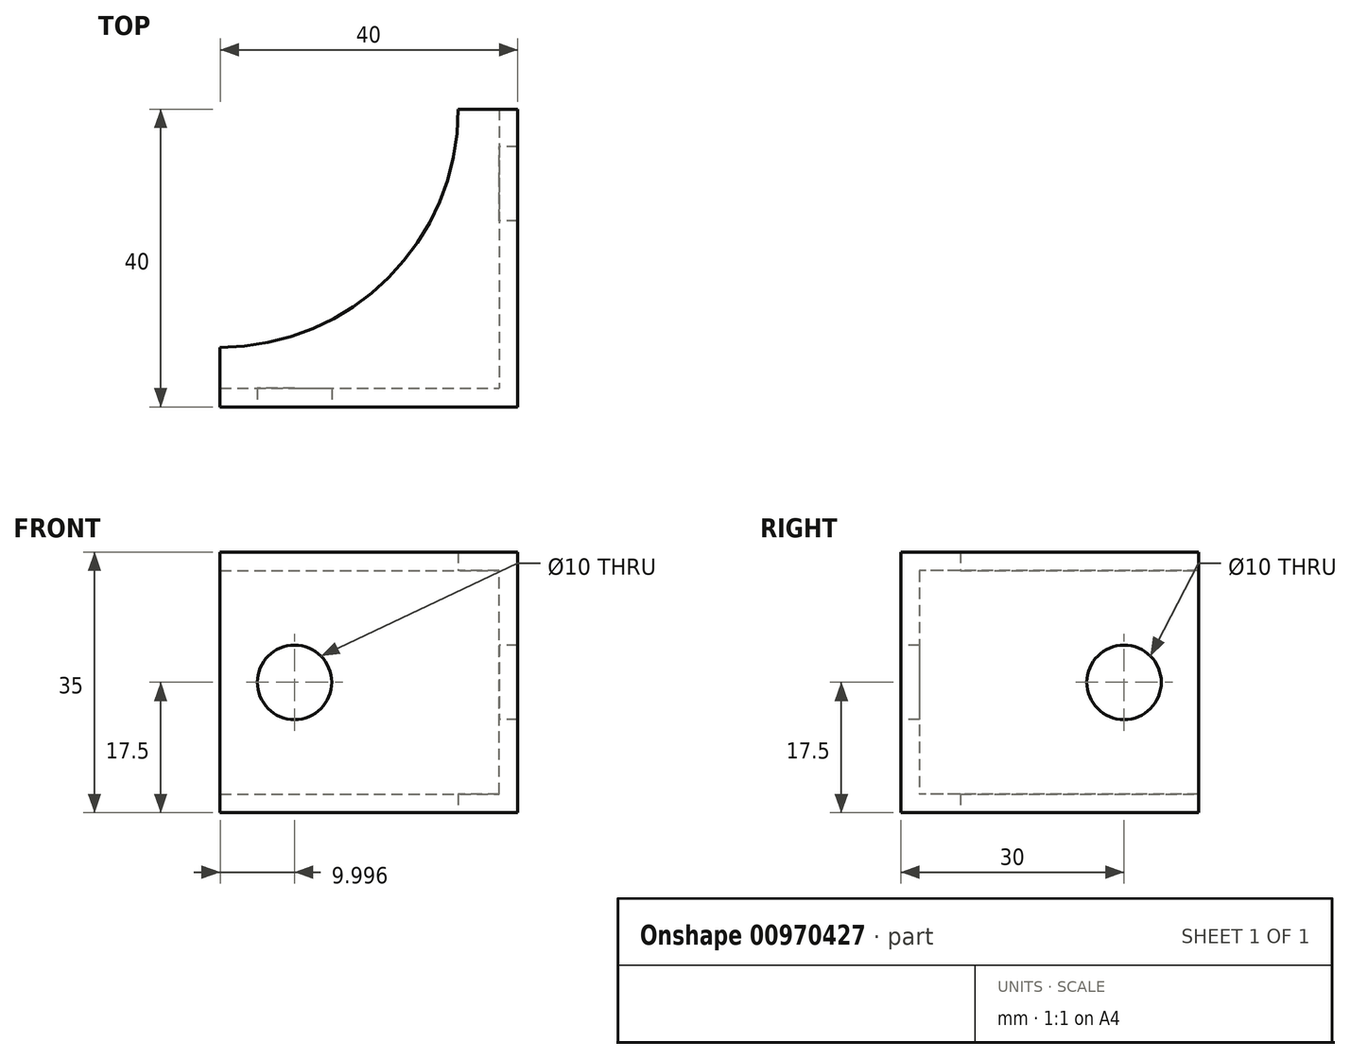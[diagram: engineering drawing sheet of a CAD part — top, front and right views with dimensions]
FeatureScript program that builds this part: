
annotation { "Feature Type Name" : "Feature", "Feature Type Description" : "" }
export const myFeature = defineFeature(function(context is Context, id is Id, definition is map)
    precondition{}
    {
        {
            var Q0;
            Q0=qCreatedBy(makeId("Top.planeOp"),FACE);
            var sketch = newSketch(context, id + "F0", { "sketchPlane" : qUnion([Q0])});
            skLineSegment(sketch, "E0.bottom", {"start": v(-29.6, 67.01) * mm, "end": v(-21.6, 67.01) * mm});
            skLineSegment(sketch, "E0.top", {"start": v(-61.6, 27.01) * mm, "end": v(-21.6, 27.01) * mm});
            skLineSegment(sketch, "E0.left", {"start": v(-61.6, 35.01) * mm, "end": v(-61.6, 27.01) * mm});
            skLineSegment(sketch, "E0.right", {"start": v(-21.6, 67.01) * mm, "end": v(-21.6, 27.01) * mm});
            skArc(sketch, "E1", {"start": v(-61.6, 35.01) * mm, "mid": v(-38.98, 44.38) * mm, "end": v(-29.6, 67.01) * mm});
            skSolve(sketch);
        }
        {
            var Q0;
            Q0=makeQuery(id+"F0.imprint","IMPRINT",FACE,{"disambiguationData":[TD([[makeQuery(id+"F0.imprint","IMPRINT",EDGE,{"derivedFrom":sQuery(id+"F0.wireOp",EDGE,"E0.bottom")}),-1.0]])]});
            extrude(context, id + "F1", {"entities" : qUnion([Q0]), "depth" : 35 * mm, "offsetDistance" : 25 * mm});
        }
        {
            var Q0;
            Q0=makeQuery(id+"F1.opExtrude","SWEPT_FACE",FACE,{"disambiguationData":[OSD([sQuery(id+"F0.wireOp",EDGE,"E1")])]});
            shell(context, id + "F2", {"entities" : qUnion([Q0]), "thickness" : 2.5 * mm});
        }
        {
            var Q0;
            Q0=makeQuery(id+"F2.opShell","OFFSET_FACE",FACE,{"disambiguationData":[OSD([sQuery(id+"F0.wireOp",EDGE,"E0.bottom")])]});
            extrude(context, id + "F3", {"entities" : qUnion([Q0]), "operationType" : NewBodyOperationType.REMOVE, "oppositeDirection" : true, "depth" : 25 * mm, "offsetDistance" : 25 * mm});
        }
        {
            var Q0;
            Q0=makeQuery(id+"F2.opShell","OFFSET_FACE",FACE,{"disambiguationData":[OSD([sQuery(id+"F0.wireOp",EDGE,"E0.left")])]});
            extrude(context, id + "F4", {"entities" : qUnion([Q0]), "operationType" : NewBodyOperationType.REMOVE, "oppositeDirection" : true, "depth" : 25 * mm, "offsetDistance" : 25 * mm});
        }
        {
            var Q0;
            {var subQ0=sQuery(id+"F0.wireOp",EDGE,"E0.right");Q0=makeQuery(id+"F3.boolean.opBoolean","MERGE",FACE,{"derivedFrom":[makeQuery(id+"F2.opShell","OFFSET_FACE",FACE,{"disambiguationData":[OSD([subQ0])]})],"fromTools":[makeQuery(id+"F3.opExtrude","SWEPT_FACE",FACE,{"disambiguationData":[OSD([sQuery(id+"F0.wireOp",EDGE,"E0.bottom"),subQ0])]})]});}
            var sketch = newSketch(context, id + "F5", { "sketchPlane" : qUnion([Q0])});
            skCircle(sketch, "E2", {"center": v(-57.01, 17.5) * mm, "radius": 5 * mm});
            skSolve(sketch);
        }
        {
            var Q0;
            Q0=sQuery(id+"F5.wireOp",VERTEX,"E2.center");
            var Q1;
            Q1=makeQuery(id+"F1.opExtrude","SWEPT_BODY",BODY,{"disambiguationData":[OSD([sQuery(id+"F0.wireOp",EDGE,"E0.bottom"),sQuery(id+"F0.wireOp",EDGE,"E0.top"),sQuery(id+"F0.wireOp",EDGE,"E0.left"),sQuery(id+"F0.wireOp",EDGE,"E0.right"),sQuery(id+"F0.wireOp",EDGE,"E1")])]});
            hole(context, id + "F6", {"style" : HoleStyle.SIMPLE, "endStyle" : HoleEndStyle.THROUGH, "holeDiameter" : 10 * mm, "majorDiameter" : 5 * mm, "isTappedThrough" : true, "tappedDepth" : 12 * mm, "tapClearance" : 3, "locations" : qUnion([Q0]), "scope" : qUnion([Q1])});
        }
        {
            var Q0;
            Q0=makeQuery(id+"F1.opExtrude","SWEPT_FACE",FACE,{"disambiguationData":[OSD([sQuery(id+"F0.wireOp",EDGE,"E0.top")])]});
            var sketch = newSketch(context, id + "F7", { "sketchPlane" : qUnion([Q0])});
            skCircle(sketch, "E3", {"center": v(-51.6, 17.5) * mm, "radius": 5 * mm});
            skSolve(sketch);
        }
        {
            var Q0;
            Q0=sQuery(id+"F7.wireOp",VERTEX,"E3.center");
            var Q1;
            Q1=makeQuery(id+"F1.opExtrude","SWEPT_BODY",BODY,{"disambiguationData":[OSD([sQuery(id+"F0.wireOp",EDGE,"E0.bottom"),sQuery(id+"F0.wireOp",EDGE,"E0.top"),sQuery(id+"F0.wireOp",EDGE,"E0.left"),sQuery(id+"F0.wireOp",EDGE,"E0.right"),sQuery(id+"F0.wireOp",EDGE,"E1")])]});
            hole(context, id + "F8", {"style" : HoleStyle.SIMPLE, "endStyle" : HoleEndStyle.THROUGH, "holeDiameter" : 10 * mm, "majorDiameter" : 5 * mm, "isTappedThrough" : true, "tappedDepth" : 12 * mm, "tapClearance" : 3, "locations" : qUnion([Q0]), "scope" : qUnion([Q1])});
        }
    });
